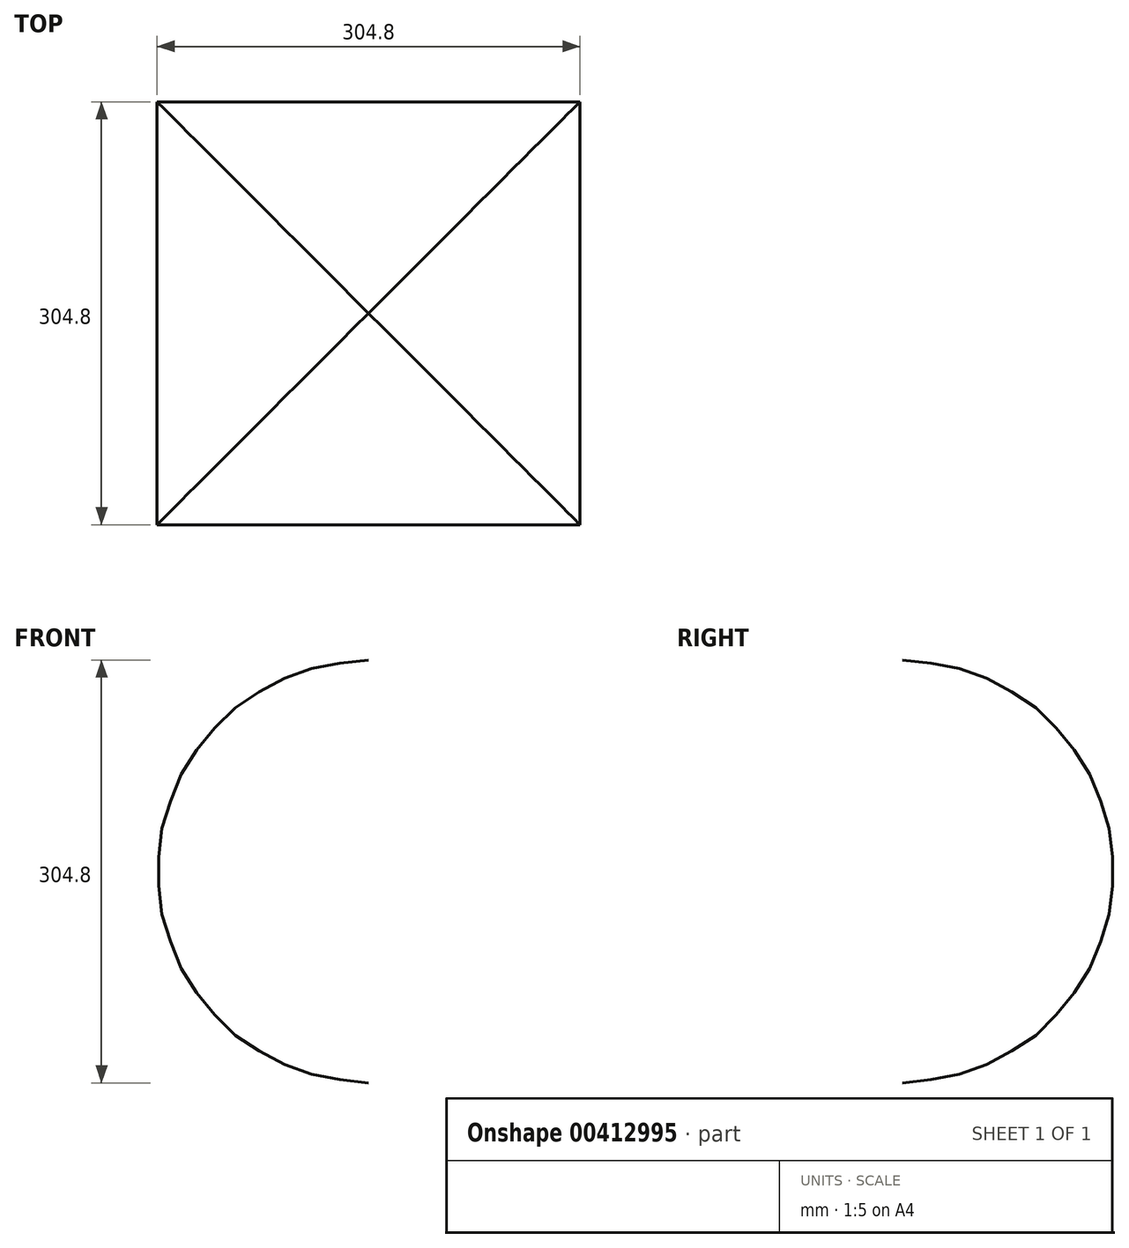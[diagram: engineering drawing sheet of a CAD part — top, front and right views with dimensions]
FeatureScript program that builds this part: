
annotation { "Feature Type Name" : "Feature", "Feature Type Description" : "" }
export const myFeature = defineFeature(function(context is Context, id is Id, definition is map)
    precondition{}
    {
        {
            var Q0;
            Q0=qCreatedBy(makeId("Top.planeOp"),FACE);
            var sketch = newSketch(context, id + "F0", { "sketchPlane" : qUnion([Q0])});
            skLineSegment(sketch, "E0.bottom", {"start": v(152.4, -152.4) * mm, "end": v(-152.4, -152.4) * mm});
            skLineSegment(sketch, "E0.top", {"start": v(152.4, 152.4) * mm, "end": v(-152.4, 152.4) * mm});
            skLineSegment(sketch, "E0.left", {"start": v(152.4, -152.4) * mm, "end": v(152.4, 152.4) * mm});
            skLineSegment(sketch, "E0.right", {"start": v(-152.4, -152.4) * mm, "end": v(-152.4, 152.4) * mm});
            skPoint(sketch, "E0.middle", {"position": v(0, 0) * mm});
            skSolve(sketch);
        }
        {
            var Q0;
            Q0=makeQuery(id+"F0.imprint","IMPRINT",FACE,{"disambiguationData":[TD([[makeQuery(id+"F0.imprint","IMPRINT",EDGE,{"derivedFrom":sQuery(id+"F0.wireOp",EDGE,"E0.bottom")}),-1.0]])]});
            extrude(context, id + "F1", {"entities" : qUnion([Q0]), "endBound" : BoundingType.SYMMETRIC, "depth" : 304.8 * mm});
        }
        {
            var Q0;
            Q0=qCreatedBy(makeId("Right.planeOp"),FACE);
            var sketch = newSketch(context, id + "F2", { "sketchPlane" : qUnion([Q0])});
            skCircle(sketch, "E1", {"center": v(0, 0) * mm, "radius": 152.4 * mm});
            skSolve(sketch);
        }
        {
            var Q0;
            Q0=qCreatedBy(makeId("Front.planeOp"),FACE);
            var sketch = newSketch(context, id + "F3", { "sketchPlane" : qUnion([Q0])});
            skCircle(sketch, "E2", {"center": v(0, 0) * mm, "radius": 152.4 * mm});
            skSolve(sketch);
        }
        {
            var Q0;
            Q0 = qSketchRegion(id + "F2", true);
            extrude(context, id + "F4", {"entities" : qUnion([Q0]), "operationType" : NewBodyOperationType.INTERSECT, "endBound" : BoundingType.SYMMETRIC, "depth" : 304.8 * mm});
        }
        {
            var Q0;
            Q0 = qSketchRegion(id + "F3", true);
            extrude(context, id + "F5", {"entities" : qUnion([Q0]), "operationType" : NewBodyOperationType.INTERSECT, "endBound" : BoundingType.SYMMETRIC, "depth" : 304.8 * mm});
        }
    });
